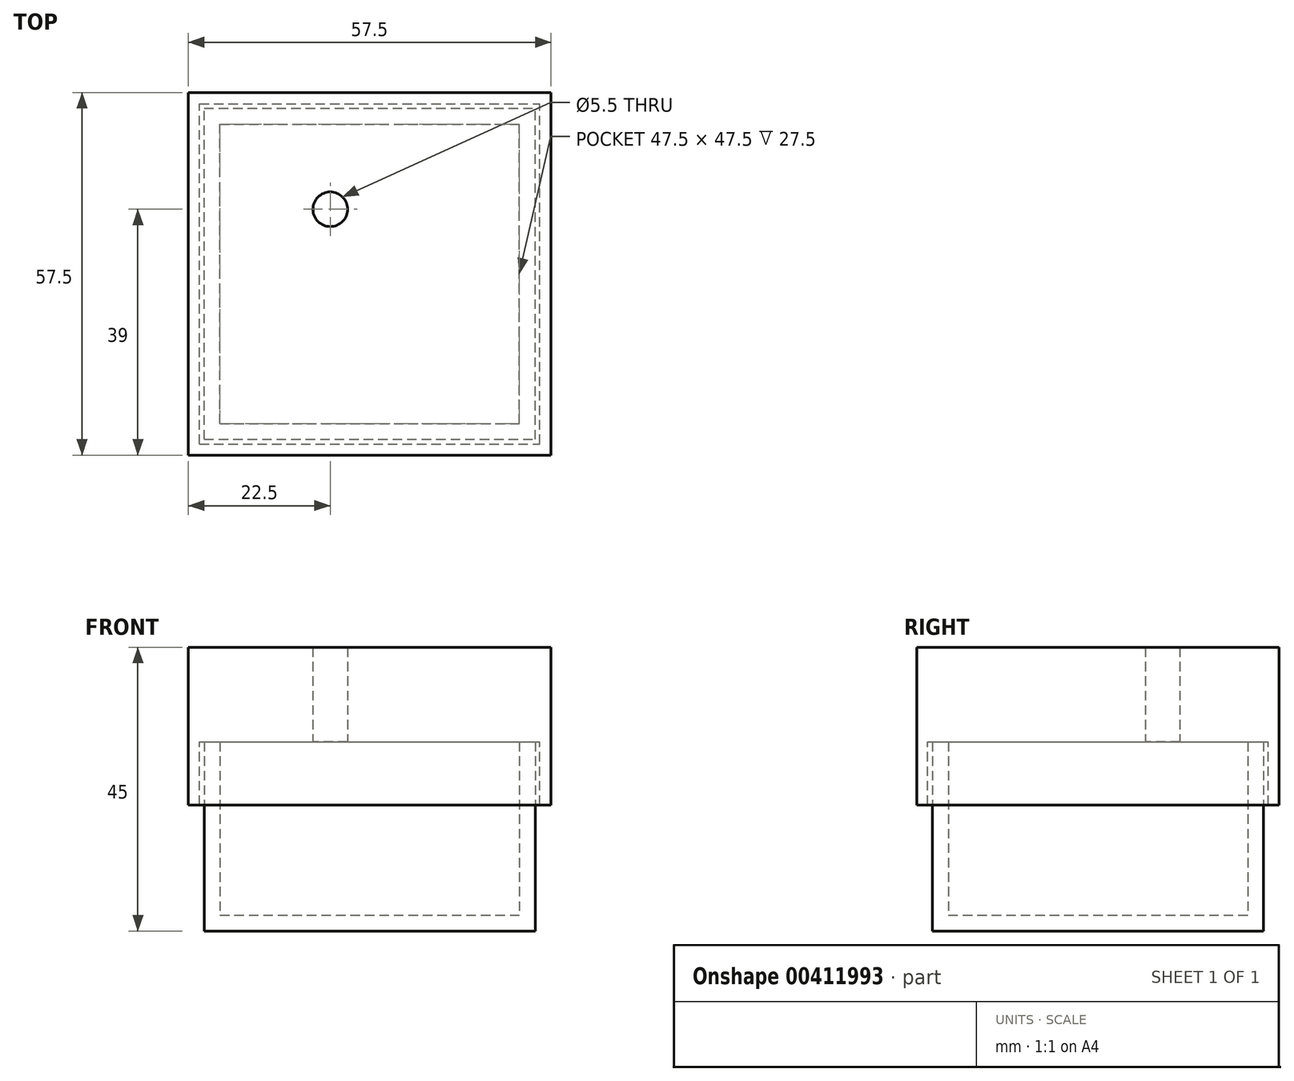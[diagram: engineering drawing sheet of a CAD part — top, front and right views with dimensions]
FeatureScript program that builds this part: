
annotation { "Feature Type Name" : "Feature", "Feature Type Description" : "" }
export const myFeature = defineFeature(function(context is Context, id is Id, definition is map)
    precondition{}
    {
        {
            var Q0;
            Q0=qCreatedBy(makeId("Top.planeOp"),FACE);
            var sketch = newSketch(context, id + "F0", { "sketchPlane" : qUnion([Q0])});
            skLineSegment(sketch, "E0.bottom", {"start": v(0, 0) * mm, "end": v(52.5, 0) * mm});
            skLineSegment(sketch, "E0.top", {"start": v(0, 52.5) * mm, "end": v(52.5, 52.5) * mm});
            skLineSegment(sketch, "E0.left", {"start": v(0, 0) * mm, "end": v(0, 52.5) * mm});
            skLineSegment(sketch, "E0.right", {"start": v(52.5, 0) * mm, "end": v(52.5, 52.5) * mm});
            skSolve(sketch);
        }
        {
            var Q0;
            Q0 = qSketchRegion(id + "F0", true);
            extrude(context, id + "F1", {"entities" : qUnion([Q0]), "depth" : 30 * mm});
        }
        {
            var Q0;
            Q0=makeQuery(id+"F1.opExtrude","CAP_FACE",FACE,{"disambiguationData":[OSD([sQuery(id+"F0.wireOp",EDGE,"E0.bottom"),sQuery(id+"F0.wireOp",EDGE,"E0.top"),sQuery(id+"F0.wireOp",EDGE,"E0.left"),sQuery(id+"F0.wireOp",EDGE,"E0.right")])],"isStart":false});
            shell(context, id + "F2", {"entities" : qUnion([Q0]), "thickness" : 2.5 * mm});
        }
        {
            var Q0;
            Q0=makeQuery(id+"F1.opExtrude","CAP_FACE",FACE,{"disambiguationData":[OSD([sQuery(id+"F0.wireOp",EDGE,"E0.bottom"),sQuery(id+"F0.wireOp",EDGE,"E0.top"),sQuery(id+"F0.wireOp",EDGE,"E0.left"),sQuery(id+"F0.wireOp",EDGE,"E0.right")])],"isStart":false});
            var sketch = newSketch(context, id + "F3", { "sketchPlane" : qUnion([Q0])});
            skLineSegment(sketch, "E1.bottom", {"start": v(2.5, 50) * mm, "end": v(50, 50) * mm});
            skLineSegment(sketch, "E1.top", {"start": v(2.5, 2.5) * mm, "end": v(50, 2.5) * mm});
            skLineSegment(sketch, "E1.left", {"start": v(2.5, 50) * mm, "end": v(2.5, 2.5) * mm});
            skLineSegment(sketch, "E1.right", {"start": v(50, 50) * mm, "end": v(50, 2.5) * mm});
            skLineSegment(sketch, "E2", {"start": v(2.5, 50) * mm, "end": v(20, 50) * mm});
            skLineSegment(sketch, "E3", {"start": v(20, 50) * mm, "end": v(20, 36.5) * mm});
            skCircle(sketch, "E4", {"center": v(20, 36.5) * mm, "radius": 2.75 * mm});
            skLineSegment(sketch, "E5.0", {"start": v(-2.5, 55) * mm, "end": v(-2.5, -2.5) * mm});
            skLineSegment(sketch, "E5.1", {"start": v(-2.5, 55) * mm, "end": v(55, 55) * mm});
            skLineSegment(sketch, "E5.2", {"start": v(55, 55) * mm, "end": v(55, -2.5) * mm});
            skLineSegment(sketch, "E5.3", {"start": v(-2.5, -2.5) * mm, "end": v(55, -2.5) * mm});
            skLineSegment(sketch, "E6.0", {"start": v(-0.75, 53.25) * mm, "end": v(53.25, 53.25) * mm});
            skLineSegment(sketch, "E6.1", {"start": v(-0.75, -0.75) * mm, "end": v(-0.75, 53.25) * mm});
            skLineSegment(sketch, "E6.2", {"start": v(-0.75, -0.75) * mm, "end": v(53.25, -0.75) * mm});
            skLineSegment(sketch, "E6.3", {"start": v(53.25, -0.75) * mm, "end": v(53.25, 53.25) * mm});
            skSolve(sketch);
        }
        {
            var Q0;
            Q0 = qSketchRegion(id + "F3", true);
            var Q1;
            Q1=makeQuery(id+"F3.imprint","IMPRINT",FACE,{"disambiguationData":[TD([[makeQuery(id+"F3.imprint","IMPRINT",EDGE,{"derivedFrom":sQuery(id+"F3.wireOp",EDGE,"E6.0")}),-1.0]])]});
            var Q2;
            Q2=makeQuery(id+"F3.imprint","IMPRINT",FACE,{"disambiguationData":[TD([[makeQuery(id+"F3.imprint","IMPRINT",EDGE,{"derivedFrom":sQuery(id+"F3.wireOp",EDGE,"E1.bottom")}),1.0]])]});
            var Q3;
            Q3=makeQuery(id+"F3.imprint","IMPRINT",FACE,{"disambiguationData":[TD([[makeQuery(id+"F3.imprint","IMPRINT",EDGE,{"derivedFrom":sQuery(id+"F3.wireOp",EDGE,"E1.bottom")}),-1.0]])]});
            extrude(context, id + "F4", {"entities" : qUnion([Q0, Q1, Q2, Q3]), "depth" : 15 * mm});
        }
        {
            var Q0;
            Q0=makeQuery(id+"F3.imprint","IMPRINT",FACE,{"disambiguationData":[TD([[makeQuery(id+"F3.imprint","IMPRINT",EDGE,{"derivedFrom":sQuery(id+"F3.wireOp",EDGE,"E5.0")}),1.0]])]});
            extrude(context, id + "F5", {"entities" : qUnion([Q0]), "operationType" : NewBodyOperationType.ADD, "oppositeDirection" : true, "depth" : 10 * mm});
        }
    });
